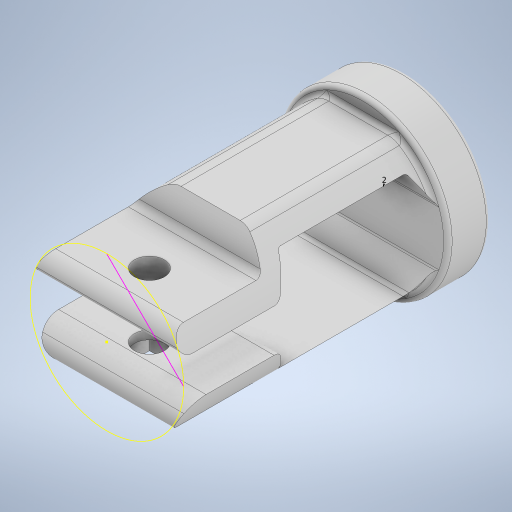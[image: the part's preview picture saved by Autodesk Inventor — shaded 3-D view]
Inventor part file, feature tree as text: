
AUTODESK INVENTOR PART (.ipt)
format: ipt  version: 2024.2 (Build 282272000, 272)  size: 516,608 bytes
history: native  units: mm
features: sketch x15, fillet x13, extrude x11, projected_geometry x1
ambient origin geometry x8: Origin, YZ Plane, XZ Plane, XY Plane, X Axis, Y Axis, Z Axis, Center Point
bodies: Solid1 (feature_tree)
feature tree (40):
  extrude  "Extrusion1"  Depth=10.0mm TaperAngle=0.0deg
  extrude  "Extrusion2"  Depth=4.0mm TaperAngle=0.0deg
  extrude  "Extrusion3"  Depth=60.0mm TaperAngle=0.0deg
  fillet  "Fillet1"  Radius=2.0mm
  fillet  "Fillet2"  Radius=1.0mm
  fillet  "Fillet3"  Radius=1.0mm
  sketch  "Sketch5"  dims[d14=0.3mm d15=0.0mm d16=6.6mm]
  extrude  "Extrusion5"  Depth=6.6mm
  extrude  "Extrusion6"  Depth=3.0mm
  extrude  "Extrusion7"  Depth=36.0mm
  extrude  "Extrusion8"  Depth=100.0mm TaperAngle=0.0deg
  extrude  "Extrusion9"  Depth=100.0mm TaperAngle=0.0deg
  extrude  "Extrusion10"  Depth=100.0mm TaperAngle=0.0deg
  fillet  "Fillet4"  Radius=7.0mm
  fillet  "Fillet5"  Radius=10.0mm
  fillet  "Fillet6"  Radius=100.0mm
  fillet  "Fillet7"  Radius=5.25mm
  fillet  "Fillet8"  Radius=5.25mm
  fillet  "Fillet9"  Radius=10.5mm
  fillet  "Fillet10"  Radius=10.5mm
  extrude  "Extrusion11"  Depth=2.0mm
  fillet  "Fillet11"  Radius=1.0mm
  extrude  "Extrusion12"  Depth=3.0mm
  fillet  "Fillet12"  Radius=6.0mm
  fillet  "Fillet13"  Radius=3.0mm
  sketch  "Sketch14"  dims[d53=36.0mm]
  sketch  "Sketch15"  dims[d54=5.0mm d55=0.0mm]
  sketch  "Sketch16"  dims[d56=1.0mm d57=3.0mm d58=6.0mm d59=5.0mm d60=0.0mm d61=1.0mm d62=5.0mm d63=2.0mm d64=0.0mm d65=0.872665mm d66=0.5mm d67=0.872665mm]
  sketch  "Sketch1"  dims[d0=40.0mm d1=10.0mm d2=0.0mm]
  sketch  "Sketch2"  dims[d3=34.0mm d4=4.0mm d5=0.0mm]
  sketch  "Sketch3"  dims[d6=36.0mm d7=60.0mm d8=0.0mm d9=2.0mm d10=1.0mm d11=1.0mm]
  projected_geometry  "Projected Loop1"
  sketch  "Sketch6"  dims[d17=12.34mm d18=3.0mm]
  sketch  "Sketch7"  dims[d19=30.0mm d20=36.0mm]
  sketch  "Sketch8"  dims[d21=5.0mm d22=100.0mm d23=100.0mm d24=0.0mm d25=0.0mm]
  sketch  "Sketch9"  dims[d26=5.0mm d27=100.0mm d28=111.0mm d29=0.0mm d30=0.0mm]
  sketch  "Sketch10"  dims[d31=7.0mm d32=100.0mm d33=111.0mm d34=0.0mm d35=0.0mm d36=7.0mm d37=10.0mm d38=100.0mm d39=0.0mm d40=5.25mm d41=5.25mm d42=10.5mm d43=10.5mm]
  sketch  "Sketch11"  dims[d44=5.0mm d45=0.0mm d46=2.0mm d47=1.0mm]
  sketch  "Sketch12"  dims[d48=3.0mm d49=3.0mm d50=6.0mm d51=3.0mm]
  sketch  "Sketch13"  dims[d52=2.0mm]
